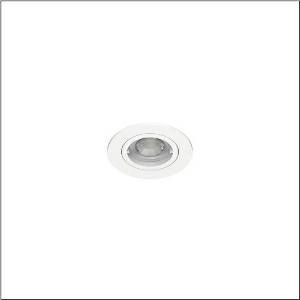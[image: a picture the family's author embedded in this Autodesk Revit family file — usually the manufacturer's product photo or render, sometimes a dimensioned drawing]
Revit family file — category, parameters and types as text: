
# Revit family: lunis_41_spot_51dt137a32a
name_source: partatom
category: Lighting Fixtures
units: mm (PartAtom-declared; Revit-internal decimal feet)

## family parameters
Cut with Voids When Loaded = No
Host = Face
Light Source = No
Part Type = Normal
Room Calculation Point = No
Round Connector Dimension = Use Diameter
Shared = No

## types (1)
- Lunis 41 Spot (1 x LED, 650 lm, 6.5 W, 3000K)
    Apparent Load = 7 VA
    CIE Flux Codes = 87 97 99 100 100
    Color Rendering = 80
    Color Temperature = 3000K
    Default Elevation = 1800 mm
    Description = Lunis 41,  Spot, downlight, light emission: direct distribution, LED rated luminous flux: 650lm, light colour: 830, control gear: ECG, mains connection: 230V, AC, 50/60Hz, housing, round, of aluminium, coated, traffic white (RAL 9016), diameter: 88mm, recess depth: 54mm, protection rating (complete): IP20, insulation class (complete): insulation class II (safety insulation), certification: CE, permissible ambient temperature for indoor applications: -20..+40°C, packaging unit: 1 piece
    Height = 0 mm  [stored 0 ft]
    Lamp = 1 x LED
    Lamp Light Flux = 650 lm
    Lamp Power = 6.5 W
    Lamp count = 1
    Length = 88 mm
    Luminous efficacy = 100 lm/W
    Manufacturer = Siteco
    ModVariant = No
    Model = 51DT137A32A
    Mounting Place = Ceiling
    Mounting Type = Recessed
    Number of Poles = 1
    OnlyDefault = Yes
    Power Factor = 1
    Product Name = Lunis 41 Spot
    Product group = downlight | ceiling recessed
    ProductGroupID = 402
    Protection Class = Protection class II
    Protection Degree = IP 20
    RLX_Detail_Level = 1
    RlxData = <blob elided: 37981 chars, md5=a2131996>
    Socket = socket
    Standby Power = 0 W
    System Light Flux = 650 lm
    System Power = 7 W
    Type Comments = Product without accessories
    Type Image = l_1005286.jpg
    URL = http://relux.com
    VarID = ---
    Voltage = 0 V
    Weight = 0.00 kg
    Width = 0 mm  [stored 0 ft]

note: [stored X ft] marks values corroborated as IEEE doubles in the binary element streams (Revit-internal decimal feet)

## geometry (parser evidence)
native form markers: Blend x4, Sweep x10
no freeform markers — native parametric forms only
